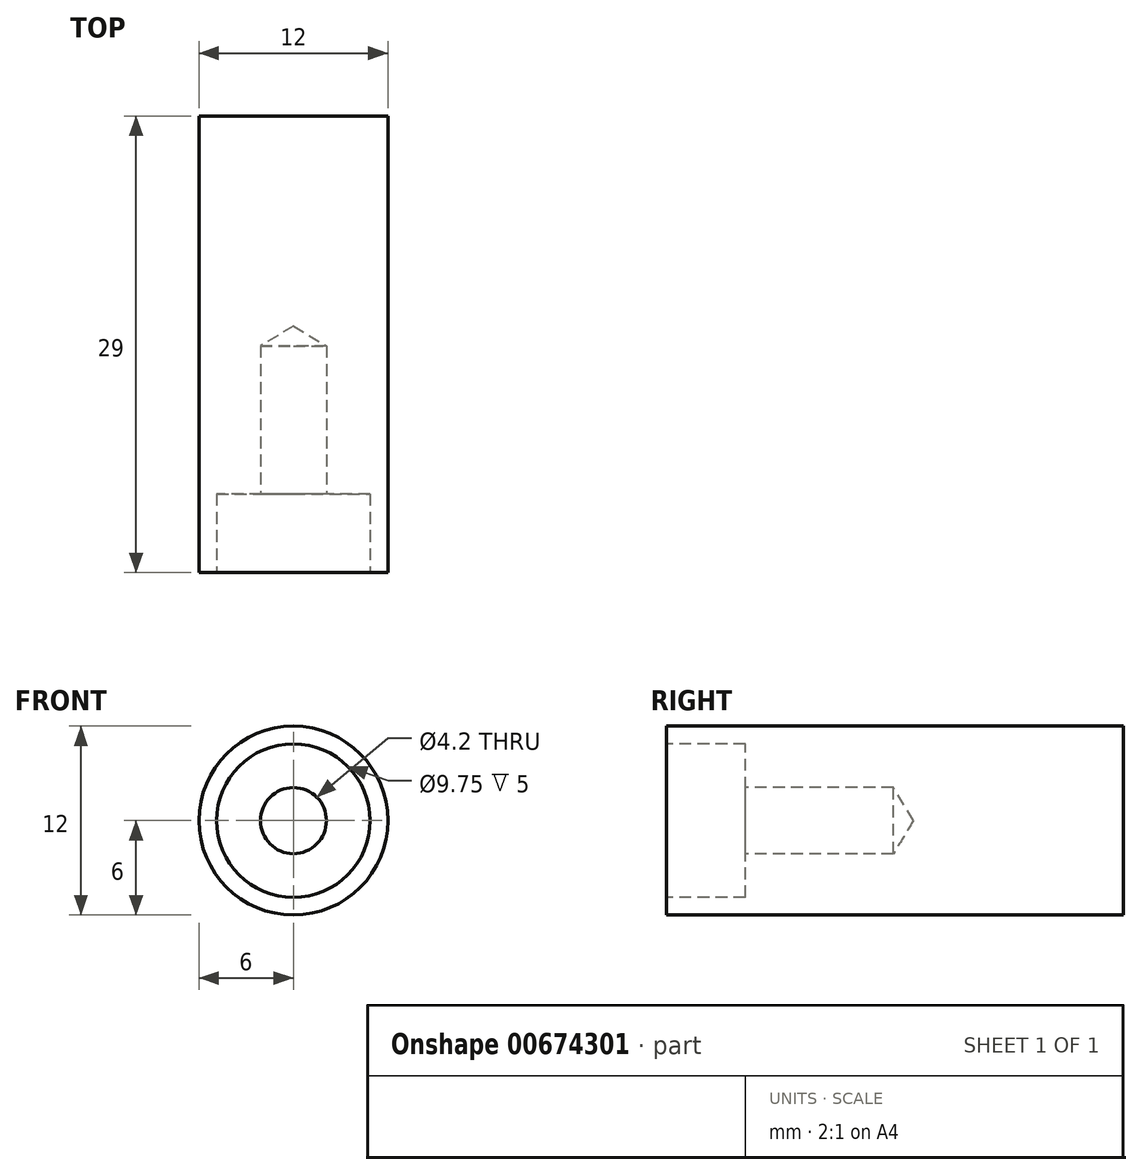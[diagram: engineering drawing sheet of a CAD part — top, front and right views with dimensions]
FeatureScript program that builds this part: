
annotation { "Feature Type Name" : "Feature", "Feature Type Description" : "" }
export const myFeature = defineFeature(function(context is Context, id is Id, definition is map)
    precondition{}
    {
        {
            var Q0;
            Q0=qCreatedBy(makeId("Front.planeOp"),FACE);
            var sketch = newSketch(context, id + "F0", { "sketchPlane" : qUnion([Q0])});
            skCircle(sketch, "E0", {"center": v(0, 0) * mm, "radius": 6 * mm});
            skSolve(sketch);
        }
        {
            var Q0;
            Q0 = qSketchRegion(id + "F0", true);
            extrude(context, id + "F1", {"entities" : qUnion([Q0]), "depth" : 29 * mm, "offsetDistance" : 25 * mm});
        }
        {
            var Q0;
            Q0=makeQuery(id+"F1.opExtrude","CAP_FACE",FACE,{"disambiguationData":[OSD([sQuery(id+"F0.wireOp",EDGE,"E0")])],"isStart":false});
            var sketch = newSketch(context, id + "F2", { "sketchPlane" : qUnion([Q0])});
            skPoint(sketch, "E1", {"position": v(0, 0) * mm});
            skSolve(sketch);
        }
        {
            var Q0;
            Q0=sQuery(id+"F2.wireOp",VERTEX,"E1");
            var Q1;
            Q1=makeQuery(id+"F1.opExtrude","SWEPT_BODY",BODY,{"disambiguationData":[OSD([sQuery(id+"F0.wireOp",EDGE,"E0")])]});
            hole(context, id + "F3", {"style" : HoleStyle.C_BORE, "endStyle" : HoleEndStyle.BLIND, "standardTappedOrClearance" : lookupTablePath({ "standard" : "ISO", "engagement" : "75%", "pitch" : "0.8 mm", "size" : "M5", "type" : "Tapped" }), "standardBlindInLast" : lookupTablePath({ "standard" : "ISO", "engagement" : "75%", "pitch" : "0.8 mm", "size" : "M5", "type" : "Tapped" }), "holeDiameter" : 4.2 * mm, "cBoreDiameter" : 9.75 * mm, "cBoreDepth" : 5 * mm, "majorDiameter" : 5 * mm, "showTappedDepth" : true, "holeDepth" : 14.4 * mm, "isTappedThrough" : true, "tappedDepth" : 12 * mm, "tapClearance" : 3, "startFromSketch" : true, "locations" : qUnion([Q0]), "scope" : qUnion([Q1])});
        }
    });
